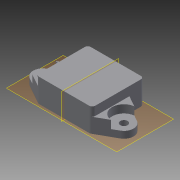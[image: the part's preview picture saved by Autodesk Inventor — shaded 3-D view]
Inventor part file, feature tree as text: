
AUTODESK INVENTOR PART (.ipt)
format: ipt  version: 2015 (Build 190159000, 159)  size: 137,216 bytes
history: native  units: mm
features: sketch x5, hole x3, extrude x2, fillet x1, mirror x1, projected_geometry x1
ambient origin geometry x8: Origin, YZ Plane, XZ Plane, XY Plane, X Axis, Y Axis, Z Axis, Center Point
bodies: Solid1 (feature_tree)
feature tree (13):
  extrude  "Extrusion1"  Depth=35.0mm
  fillet  "Fillet1"  Radius=16.0mm
  extrude  "Extrusion2"  Depth=2.0mm
  hole  "Hole1"  [1 undecoded]
  mirror  "Mirror1"
  hole  "Hole2"  [1 undecoded]
  hole  "Hole3"  [1 undecoded]
  sketch  "Sketch1"  dims[d0=38.0mm d1=35.0mm d2=16.0mm d3=0.0mm]
  sketch  "Sketch2"  dims[d4=2.0mm d5=27.5mm]
  sketch  "Sketch3"  dims[d6=13.0mm d7=6.5mm]
  sketch  "Sketch4"  dims[d8=5.082332mm d9=5.082332mm]
  projected_geometry  "Projected Loop1"
  sketch  "Sketch5"  dims[d10=10.0mm d11=0.0mm d12=16.0mm d13=6.0mm d14=4.0mm d15=2.0mm d16=90.0deg d17=5.4mm d18=0.0mm d19=5.0mm d20=34.925mm d21=4.0mm d22=2.0mm d23=90.0deg d24=5.4mm d25=0.0mm d26=4.5mm d27=34.925mm d28=4.0mm d29=2.0mm d30=90.0deg d31=5.4mm d32=0.0mm]
note: 3 required parameter values undecoded (feature->parameter linkage not recoverable at this tier; creation-order binding heuristic only, values carry confidence <= 0.55)
